FCSTD DOCUMENT  (FreeCAD 0.19R24366 (Git))
Label: Pi and controller board V2 prototype front panel
License: All rights reserved
LicenseURL: http://en.wikipedia.org/wiki/All_rights_reserved
objects: Sketcher::SketchObject×1, PartDesign::Body×1
note: 2 computed .brp shape members not serialized (recipe doc carries the construction recipe); baked Part::Feature solids carry a one-line shape summary decoded from their .brp

FEATURE [Sketcher::SketchObject] Sketch
  FullyConstrained = true
  MapMode = 5
  Support = -> [XY_Plane]
  sketch-geometry (56):
    g0: LineSegment StartX=-180 StartY=26 StartZ=0 EndX=-180 EndY=-13 EndZ=0
    g1: LineSegment StartX=-170 StartY=36 StartZ=0 EndX=170 EndY=36 EndZ=0
    g2: LineSegment StartX=180 StartY=26 StartZ=0 EndX=180 EndY=-13 EndZ=0
    g3: LineSegment StartX=180 StartY=-13 StartZ=0 EndX=-180 EndY=-13 EndZ=0
    g4: ArcOfCircle CenterX=170 CenterY=26 CenterZ=0 NormalX=0 NormalY=0 NormalZ=1 AngleXU=0 Radius=10 StartAngle=0 EndAngle=1.5708
    g5: ArcOfCircle CenterX=-170 CenterY=26 CenterZ=0 NormalX=0 NormalY=0 NormalZ=1 AngleXU=0 Radius=10 StartAngle=1.5708 EndAngle=3.14159
    g6: ArcOfCircle CenterX=-137 CenterY=13 CenterZ=0 NormalX=0 NormalY=0 NormalZ=1 AngleXU=0 Radius=7.95 StartAngle=3.23923 EndAngle=9.32714
    g7: Circle CenterX=-104 CenterY=13 CenterZ=0 NormalX=0 NormalY=0 NormalZ=1 AngleXU=0 Radius=3.5
    g8: LineSegment StartX=-137 StartY=13 StartZ=0 EndX=-104 EndY=13 EndZ=0
    g9: LineSegment StartX=150 StartY=36 StartZ=0 EndX=150 EndY=-10 EndZ=0
    g10: LineSegment StartX=-83.856 StartY=36 StartZ=0 EndX=-83.856 EndY=-10 EndZ=0
    g11: GeomPoint X=-180 Y=-10 Z=0
    g12: LineSegment StartX=-180 StartY=-10 StartZ=0 EndX=180 EndY=-10 EndZ=0
    g13: LineSegment StartX=-104 StartY=13 StartZ=0 EndX=-83.856 EndY=13 EndZ=0
    g14: Circle CenterX=-104 CenterY=13 CenterZ=0 NormalX=0 NormalY=0 NormalZ=1 AngleXU=0 Radius=8.5
    g15: Circle CenterX=-137 CenterY=13 CenterZ=0 NormalX=0 NormalY=0 NormalZ=1 AngleXU=0 Radius=12
    g16: LineSegment StartX=-137 StartY=13 StartZ=0 EndX=-180 EndY=13 EndZ=0
    g17: LineSegment StartX=-112.45 StartY=14.5 StartZ=0 EndX=-111.15 EndY=14.5 EndZ=0
    g18: LineSegment StartX=-111.15 StartY=14.5 StartZ=0 EndX=-111.15 EndY=11.5 EndZ=0
    g19: LineSegment StartX=-111.15 StartY=11.5 StartZ=0 EndX=-112.45 EndY=11.5 EndZ=0
    g20: LineSegment StartX=-112.45 StartY=11.5 StartZ=0 EndX=-112.45 EndY=14.5 EndZ=0
    g21: GeomPoint X=-111.8 Y=11.5 Z=0
    g22: LineSegment StartX=114 StartY=1 StartZ=0 EndX=130 EndY=1 EndZ=0
    g23: LineSegment StartX=130 StartY=1 StartZ=0 EndX=130 EndY=-9 EndZ=0
    g24: LineSegment StartX=130 StartY=-9 StartZ=0 EndX=114 EndY=-9 EndZ=0
    g25: LineSegment StartX=114 StartY=-9 StartZ=0 EndX=114 EndY=1 EndZ=0
    g26: GeomPoint X=122 Y=-9 Z=0
    g27: GeomPoint X=130 Y=-4 Z=0
    g28: LineSegment StartX=-36.972 StartY=33 StartZ=0 EndX=45.028 EndY=33 EndZ=0
    g29: LineSegment StartX=45.028 StartY=33 StartZ=0 EndX=45.028 EndY=-7 EndZ=0
    g30: LineSegment StartX=45.028 StartY=-7 StartZ=0 EndX=-36.972 EndY=-7 EndZ=0
    g31: LineSegment StartX=-36.972 StartY=-7 StartZ=0 EndX=-36.972 EndY=33 EndZ=0
    g32: GeomPoint X=4.028 Y=-7 Z=0
    g33: GeomPoint X=45.028 Y=13 Z=0
    g34: GeomPoint X=150 Y=13 Z=0
    g35: LineSegment StartX=45.028 StartY=13 StartZ=0 EndX=150 EndY=13 EndZ=0
    g36: LineSegment StartX=-144.912 StartY=13.775 StartZ=0 EndX=-144.2 EndY=13.775 EndZ=0
    g37: LineSegment StartX=-144.2 StartY=13.775 StartZ=0 EndX=-144.2 EndY=12.225 EndZ=0
    g38: LineSegment StartX=-144.2 StartY=12.225 StartZ=0 EndX=-144.912 EndY=12.225 EndZ=0
    g39: LineSegment StartX=-160 StartY=-13 StartZ=0 EndX=-160 EndY=-33 EndZ=0
    g40: LineSegment StartX=160 StartY=-13 StartZ=0 EndX=160 EndY=-33 EndZ=0
    g41: LineSegment StartX=180 StartY=-13 StartZ=0 EndX=180 EndY=-33 EndZ=0
    g42: LineSegment StartX=-180 StartY=-13 StartZ=0 EndX=-180 EndY=-33 EndZ=0
    g43: LineSegment StartX=180 StartY=-33 StartZ=0 EndX=-180 EndY=-33 EndZ=0
    g44: Circle CenterX=-170 CenterY=-23 CenterZ=0 NormalX=0 NormalY=0 NormalZ=1 AngleXU=0 Radius=3.25
    g45: Circle CenterX=170 CenterY=-23 CenterZ=0 NormalX=0 NormalY=0 NormalZ=1 AngleXU=0 Radius=3.25
    g46: ArcOfCircle CenterX=-104 CenterY=31 CenterZ=0 NormalX=0 NormalY=0 NormalZ=1 AngleXU=0 Radius=1.15 StartAngle=0 EndAngle=3.14159
    g47: ArcOfCircle CenterX=-104 CenterY=19 CenterZ=0 NormalX=0 NormalY=0 NormalZ=1 AngleXU=0 Radius=1.15 StartAngle=3.14159 EndAngle=6.28319
    g48: LineSegment StartX=-105.15 StartY=31 StartZ=0 EndX=-105.15 EndY=19 EndZ=0
    g49: LineSegment StartX=-102.85 StartY=31 StartZ=0 EndX=-102.85 EndY=19 EndZ=0
    g50: ArcOfCircle CenterX=-104 CenterY=7 CenterZ=0 NormalX=0 NormalY=0 NormalZ=1 AngleXU=0 Radius=1.15 StartAngle=0 EndAngle=3.14159
    g51: ArcOfCircle CenterX=-104 CenterY=-5 CenterZ=0 NormalX=0 NormalY=0 NormalZ=1 AngleXU=0 Radius=1.15 StartAngle=3.14159 EndAngle=6.28319
    g52: LineSegment StartX=-105.15 StartY=7 StartZ=0 EndX=-105.15 EndY=-5 EndZ=0
    g53: LineSegment StartX=-102.85 StartY=7 StartZ=0 EndX=-102.85 EndY=-5 EndZ=0
    g54: LineSegment StartX=-104 StartY=13 StartZ=0 EndX=-104 EndY=19 EndZ=0
    g55: LineSegment StartX=-104 StartY=13 StartZ=0 EndX=-104 EndY=7 EndZ=0
  constraints (144):
    c: Vertical(g0)
    c: Horizontal(g1)
    c: Vertical(g2)
    c: Tangent(g1,g4) = 1.5708
    c: Tangent(g2,g4) = 1.5708
    c: Tangent(g1,g5) = 1.5708
    c: Tangent(g0,g5) = -1.5708
    c: Radius(g5) = 10
    c: Coincident(g8,g6)
    c: Coincident(g8,g7)
    c: Horizontal(g8)
    c: Diameter(g7) = 7
    c: Diameter(g6) = 15.9
    c: PointOnObject(g9,g1)
    c: Vertical(g9)
    c: PointOnObject(g10,g1)
    c: Vertical(g10)
    c: PointOnObject(g11,g0)
    c: Coincident(g0,g3)
    c: DistanceY(g0,g11) = 3
    c: DistanceY(g11,g1) = 46
    c: Coincident(g2,g3)
    c: Coincident(g12,g11)
    c: PointOnObject(g12,g2)
    c: Horizontal(g12)
    c: PointOnObject(g9,g12)
    c: PointOnObject(g10,g12)
    c: DistanceX(g10,g9) = 233.856
    c: Coincident(g13,g7)
    c: Horizontal(g13)
    c: Symmetric(g10,g10,g13)
    c: Coincident(g14,g7)
    c: Diameter(g14) = 17
    c: Coincident(g15,g6)
    c: Diameter(g15) = 24
    c: DistanceX(g6,g7) = 33
    c: DistanceX(g0,g2) = 360
    c: Coincident(g16,g6)
    c: PointOnObject(g16,g0)
    c: Horizontal(g16)
    c: DistanceX(g0,g6) = 43
    c: DistanceX(g7,g13) = 20.144
    c: Symmetric(g0,g2,g-2)
    c: Equal(g4,g5)
    c: Coincident(g17,g18)
    c: Coincident(g18,g19)
    c: Coincident(g19,g20)
    c: Coincident(g20,g17)
    c: Horizontal(g17)
    c: Horizontal(g19)
    c: Vertical(g18)
    c: Symmetric(g17,g19,g8)
    c: DistanceX(g19,g19) = 1.3
    c: DistanceY(g20,g20) = 3
    c: Symmetric(g19,g18,g21)
    c: DistanceX(g21,g7) = 7.8
    c: Coincident(g22,g23)
    c: Coincident(g23,g24)
    c: Coincident(g24,g25)
    c: Coincident(g25,g22)
    c: Horizontal(g22)
    c: Horizontal(g24)
    c: Vertical(g23)
    c: Vertical(g25)
    c: Symmetric(g24,g23,g26)
    c: DistanceX(g26,g9) = 28
    c: DistanceX(g24,g24) = 16
    c: Symmetric(g23,g22,g27)
    c: DistanceY(g12,g27) = 6
    c: DistanceY(g25,g25) = 10
    c: Coincident(g28,g29)
    c: Coincident(g29,g30)
    c: Coincident(g30,g31)
    c: Coincident(g31,g28)
    c: Horizontal(g28)
    c: Horizontal(g30)
    c: Vertical(g29)
    c: Vertical(g31)
    c: Symmetric(g29,g30,g32)
    c: DistanceX(g32,g9) = 145.972
    c: DistanceX(g30,g30) = 82
    c: DistanceY(g31,g31) = 40
    c: Coincident(g35,g33)
    c: Coincident(g35,g34)
    c: Horizontal(g35)
    c: Symmetric(g28,g29,g35)
    c: Symmetric(g9,g9,g35)
    c: Coincident(g36,g6)
    c: Coincident(g37,g36)
    c: Coincident(g38,g37)
    c: Coincident(g38,g6)
    c: Horizontal(g38)
    c: Horizontal(g36)
    c: Symmetric(g36,g37,g16)
    c: DistanceY(g37,g37) = 1.55
    c: DistanceX(g37,g6) = 7.2
    c: PointOnObject(g39,g3)
    c: Vertical(g39)
    c: PointOnObject(g40,g3)
    c: Vertical(g40)
    c: Coincident(g41,g2)
    c: Vertical(g41)
    c: Coincident(g42,g0)
    c: Equal(g39,g41)
    c: Coincident(g43,g41)
    c: Coincident(g43,g42)
    c: Horizontal(g43)
    c: PointOnObject(g40,g43)
    c: DistanceX(g40,g41) = 20
    c: DistanceX(g42,g39) = 20
    c: Vertical(g42)
    c: DistanceX(g45,g2) = 10
    c: DistanceX(g0,g44) = 10
    c: Diameter(g44) = 6.5
    c: Equal(g44,g45)
    c: DistanceY(g44,g0) = 10
    c: DistanceY(g45,g2) = 10
    c: DistanceY(g42,g0) = 20
    c: DistanceX(g9,g45) = 20
    c: DistanceY(g11,g-1) = 10
    c: Tangent(g46,g49) = 1.5708
    c: Tangent(g46,g48) = -1.5708
    c: Tangent(g48,g47) = -1.5708
    c: Tangent(g49,g47) = 1.5708
    c: Vertical(g48)
    c: Equal(g46,g47)
    c: Tangent(g50,g53) = 1.5708
    c: Tangent(g50,g52) = -1.5708
    c: Tangent(g52,g51) = -1.5708
    c: Tangent(g53,g51) = 1.5708
    c: Vertical(g52)
    c: Equal(g50,g51)
    c: Coincident(g54,g7)
    c: Coincident(g54,g47)
    c: Coincident(g55,g7)
    c: Coincident(g55,g50)
    c: Vertical(g54)
    c: Vertical(g55)
    c: Equal(g47,g50)
    c: Diameter(g47) = 2.3
    c: DistanceY(g54,g54) = 6
    c: Equal(g54,g55)
    c: Equal(g53,g49)
    c: DistanceY(g49,g49) = 12
FEATURE [PartDesign::Body] Body
  Group = -> [Sketch]
  Origin = -> Origin
